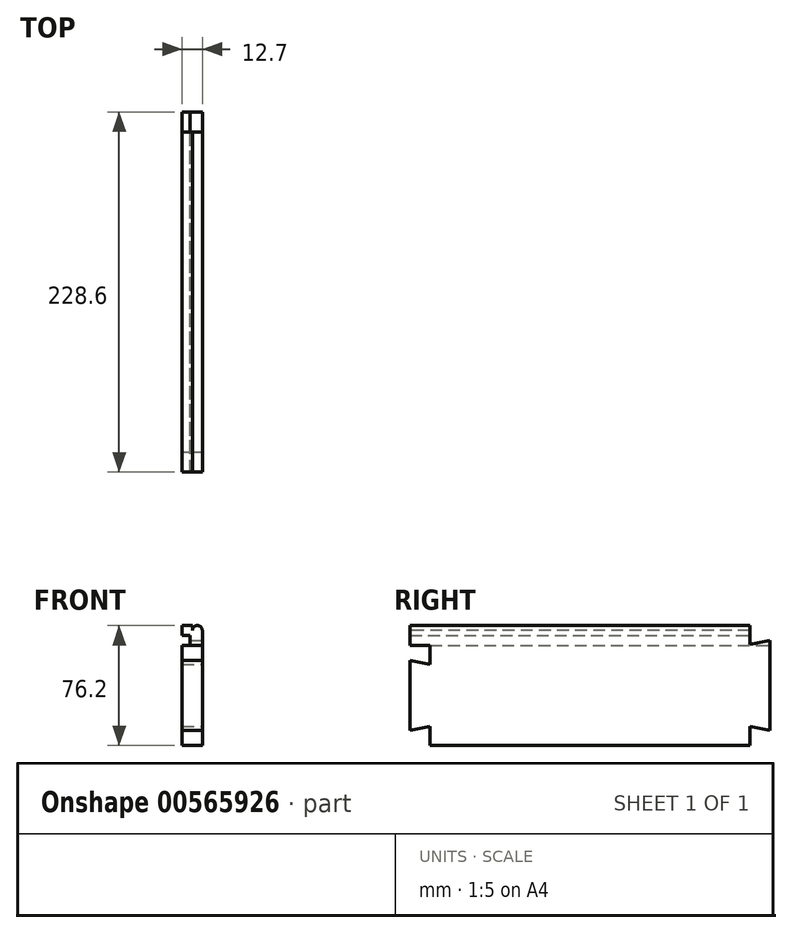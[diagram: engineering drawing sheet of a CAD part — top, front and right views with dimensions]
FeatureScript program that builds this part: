
annotation { "Feature Type Name" : "Feature", "Feature Type Description" : "" }
export const myFeature = defineFeature(function(context is Context, id is Id, definition is map)
    precondition{}
    {
        {
            var Q0;
            Q0=qCreatedBy(makeId("Front.planeOp"),FACE);
            var sketch = newSketch(context, id + "F0", { "sketchPlane" : qUnion([Q0])});
            skLineSegment(sketch, "E0.bottom", {"start": v(-6.35, 38.1) * mm, "end": v(6.35, 38.1) * mm});
            skLineSegment(sketch, "E0.top", {"start": v(-6.35, -38.1) * mm, "end": v(6.35, -38.1) * mm});
            skLineSegment(sketch, "E0.left", {"start": v(-6.35, 38.1) * mm, "end": v(-6.35, -38.1) * mm});
            skLineSegment(sketch, "E0.right", {"start": v(6.35, 38.1) * mm, "end": v(6.35, -38.1) * mm});
            skLineSegment(sketch, "E1", {"start": v(-6.35, 38.1) * mm, "end": v(6.35, -38.1) * mm, "construction": true});
            skSolve(sketch);
        }
        {
            var Q0;
            Q0=qSketchRegion(id+"F0",true);
            extrude(context, id + "F1", {"entities" : qUnion([Q0]), "endBound" : BoundingType.SYMMETRIC, "depth" : 228.6 * mm, "offsetDistance" : 25.4 * mm});
        }
        {
            var Q0;
            {var subQ0=sQuery(id+"F0.wireOp",EDGE,"E0.right");var subQ2=sQuery(id+"F0.wireOp",EDGE,"E0.top");var subQ5=makeQuery(id+"F5.opExtrude","SWEPT_FACE",FACE,{"disambiguationData":[OSD([sQuery(id+"F4.wireOp",EDGE,"E23.0")])]});Q0=makeQuery(id+"FtgXUjz83fswi7n_1.boolean.opBoolean","SPLIT",FACE,{"disambiguationData":[TD([makeQuery(id+"F5.boolean.opBoolean","COPY",FACE,{"derivedFrom":subQ5})])],"derivedFrom":makeQuery(id+"F5.boolean.opBoolean","SPLIT",FACE,{"disambiguationData":[TD([makeQuery(id+"F1.opExtrude","SWEPT_FACE",FACE,{"disambiguationData":[OSD([subQ2])]})])],"derivedFrom":makeQuery(id+"F1.opExtrude","SWEPT_FACE",FACE,{"disambiguationData":[OSD([subQ0])]})})});}
            var sketch = newSketch(context, id + "F2", { "sketchPlane" : qUnion([Q0])});
            skLineSegment(sketch, "E2", {"start": v(-114.3, 25.4) * mm, "end": v(-101.6, 25.4) * mm});
            skLineSegment(sketch, "E3", {"start": v(-114.3, 25.4) * mm, "end": v(-114.3, 15.87) * mm});
            skLineSegment(sketch, "E4", {"start": v(-114.3, 15.87) * mm, "end": v(-101.6, 13.34) * mm});
            skLineSegment(sketch, "E5", {"start": v(-101.6, 13.34) * mm, "end": v(-101.6, 25.4) * mm});
            skLineSegment(sketch, "E6", {"start": v(-114.3, 15.87) * mm, "end": v(-81.41, 15.88) * mm, "construction": true});
            skLineSegment(sketch, "E7", {"start": v(-114.3, 25.4) * mm, "end": v(-114.3, -38.1) * mm, "construction": true});
            skLineSegment(sketch, "E8", {"start": v(-114.3, -6.35) * mm, "end": v(-42.34, -6.35) * mm, "construction": true});
            skLineSegment(sketch, "E9.MirrorCS", {"start": v(-114.3, -38.1) * mm, "end": v(-101.6, -38.1) * mm});
            skLineSegment(sketch, "E10.MirrorCS", {"start": v(-101.6, -26.04) * mm, "end": v(-101.6, -38.1) * mm});
            skLineSegment(sketch, "E11.MirrorCS", {"start": v(-114.3, -28.57) * mm, "end": v(-101.6, -26.04) * mm});
            skLineSegment(sketch, "E12.MirrorCS", {"start": v(-114.3, -38.1) * mm, "end": v(-114.3, -28.57) * mm});
            skLineSegment(sketch, "E13", {"start": v(114.3, 38.1) * mm, "end": v(101.6, 38.1) * mm});
            skLineSegment(sketch, "E14", {"start": v(114.3, 38.1) * mm, "end": v(114.3, 28.57) * mm});
            skLineSegment(sketch, "E15", {"start": v(101.6, 38.1) * mm, "end": v(101.6, 26.04) * mm});
            skLineSegment(sketch, "E16", {"start": v(101.6, 26.04) * mm, "end": v(114.3, 28.57) * mm});
            skLineSegment(sketch, "E17.MirrorCS", {"start": v(114.3, -38.1) * mm, "end": v(114.3, -28.57) * mm});
            skLineSegment(sketch, "E18.MirrorCS", {"start": v(101.6, -38.1) * mm, "end": v(101.6, -26.04) * mm});
            skLineSegment(sketch, "E19.MirrorCS", {"start": v(101.6, -26.04) * mm, "end": v(114.3, -28.57) * mm});
            skLineSegment(sketch, "E20.MirrorCS", {"start": v(114.3, -38.1) * mm, "end": v(101.6, -38.1) * mm});
            skLineSegment(sketch, "E21", {"start": v(114.3, 28.57) * mm, "end": v(83.32, 28.57) * mm, "construction": true});
            skSolve(sketch);
        }
        {
            var Q0;
            Q0=qSketchRegion(id+"F2",true);
            var Q1;
            Q1=makeQuery(id+"F1.opExtrude","SWEPT_FACE",FACE,{"disambiguationData":[OSD([sQuery(id+"F0.wireOp",EDGE,"E0.left")])]});
            extrude(context, id + "F3", {"entities" : qUnion([Q0]), "operationType" : NewBodyOperationType.REMOVE, "endBound" : BoundingType.UP_TO_SURFACE, "oppositeDirection" : true, "depth" : 25.4 * mm, "endBoundEntityFace" : qUnion([Q1]), "offsetDistance" : 25.4 * mm});
        }
        {
            var Q0;
            Q0=makeQuery(id+"F1.opExtrude","SWEPT_FACE",FACE,{"disambiguationData":[OSD([sQuery(id+"F0.wireOp",EDGE,"E0.left")])]});
            var sketch = newSketch(context, id + "F4", { "sketchPlane" : qUnion([Q0])});
            skLineSegment(sketch, "E22.0", {"start": v(114.3, 31.75) * mm, "end": v(-114.3, 31.75) * mm});
            skLineSegment(sketch, "E23.0", {"start": v(114.3, 25.4) * mm, "end": v(-114.3, 25.4) * mm});
            skLineSegment(sketch, "E24", {"start": v(114.3, 31.75) * mm, "end": v(114.3, 25.4) * mm});
            skLineSegment(sketch, "E25", {"start": v(-114.3, 31.75) * mm, "end": v(-114.3, 25.4) * mm});
            skSolve(sketch);
        }
        {
            var Q0;
            Q0=qSketchRegion(id+"F4",true);
            extrude(context, id + "F5", {"entities" : qUnion([Q0]), "operationType" : NewBodyOperationType.REMOVE, "oppositeDirection" : true, "depth" : 4.76 * mm, "offsetDistance" : 25.4 * mm});
        }
        {
            var Q0;
            {var subQ0=sQuery(id+"F0.wireOp",EDGE,"E0.top");var subQ2=sQuery(id+"F0.wireOp",EDGE,"E0.left");Q0=makeQuery(id+"F5.boolean.opBoolean","SPLIT",FACE,{"disambiguationData":[TD([makeQuery(id+"F1.opExtrude","SWEPT_FACE",FACE,{"disambiguationData":[OSD([subQ0])]})])],"derivedFrom":makeQuery(id+"F1.opExtrude","SWEPT_FACE",FACE,{"disambiguationData":[OSD([subQ2])]})});}
            var sketch = newSketch(context, id + "F6", { "sketchPlane" : qUnion([Q0])});
            skLineSegment(sketch, "E26.0", {"start": v(101.6, -33.34) * mm, "end": v(-114.3, -33.34) * mm});
            skLineSegment(sketch, "E27.0", {"start": v(101.6, -30.16) * mm, "end": v(-114.3, -30.16) * mm});
            skLineSegment(sketch, "E28", {"start": v(101.6, -30.16) * mm, "end": v(101.6, -33.34) * mm});
            skLineSegment(sketch, "E29", {"start": v(-114.3, -30.16) * mm, "end": v(-114.3, -33.34) * mm});
            skSolve(sketch);
        }
        {
            var Q0;
            {var subQ0=sQuery(id+"F0.wireOp",EDGE,"E0.bottom");var subQ1=sQuery(id+"F0.wireOp",EDGE,"E0.right");var subQ2=sQuery(id+"F0.wireOp",EDGE,"E0.left");Q0=makeQuery(id+"F3.boolean.opBoolean","SPLIT",FACE,{"disambiguationData":[TD([makeQuery(id+"F1.opExtrude","SWEPT_FACE",FACE,{"disambiguationData":[OSD([subQ0])]})])],"derivedFrom":makeQuery(id+"F1.opExtrude","CAP_FACE",FACE,{"disambiguationData":[OSD([subQ0,sQuery(id+"F0.wireOp",EDGE,"E0.top"),subQ2,subQ1])],"isStart":false})});}
            var sketch = newSketch(context, id + "F7", { "sketchPlane" : qUnion([Q0])});
            skArc(sketch, "E30", {"start": v(6.35, 34.93) * mm, "mid": v(3.18, 38.1) * mm, "end": v(0, 34.93) * mm});
            skLineSegment(sketch, "E31", {"start": v(0, 34.93) * mm, "end": v(0, 38.1) * mm});
            skLineSegment(sketch, "E32", {"start": v(6.35, 34.93) * mm, "end": v(6.35, 38.1) * mm});
            skLineSegment(sketch, "E33", {"start": v(6.35, 38.1) * mm, "end": v(0, 38.1) * mm});
            skSolve(sketch);
        }
        {
            var Q0;
            Q0 = qSketchRegion(id + "F7", true);
            var Q1;
            Q1=makeQuery(id+"F3.boolean.opBoolean","COPY",FACE,{"derivedFrom":makeQuery(id+"F3.opExtrude","SWEPT_FACE",FACE,{"disambiguationData":[OSD([sQuery(id+"F2.wireOp",EDGE,"E15")])]})});
            extrude(context, id + "F8", {"entities" : qUnion([Q0]), "operationType" : NewBodyOperationType.REMOVE, "endBound" : BoundingType.UP_TO_SURFACE, "oppositeDirection" : true, "depth" : 25.4 * mm, "endBoundEntityFace" : qUnion([Q1]), "offsetDistance" : 25.4 * mm});
        }
    });
